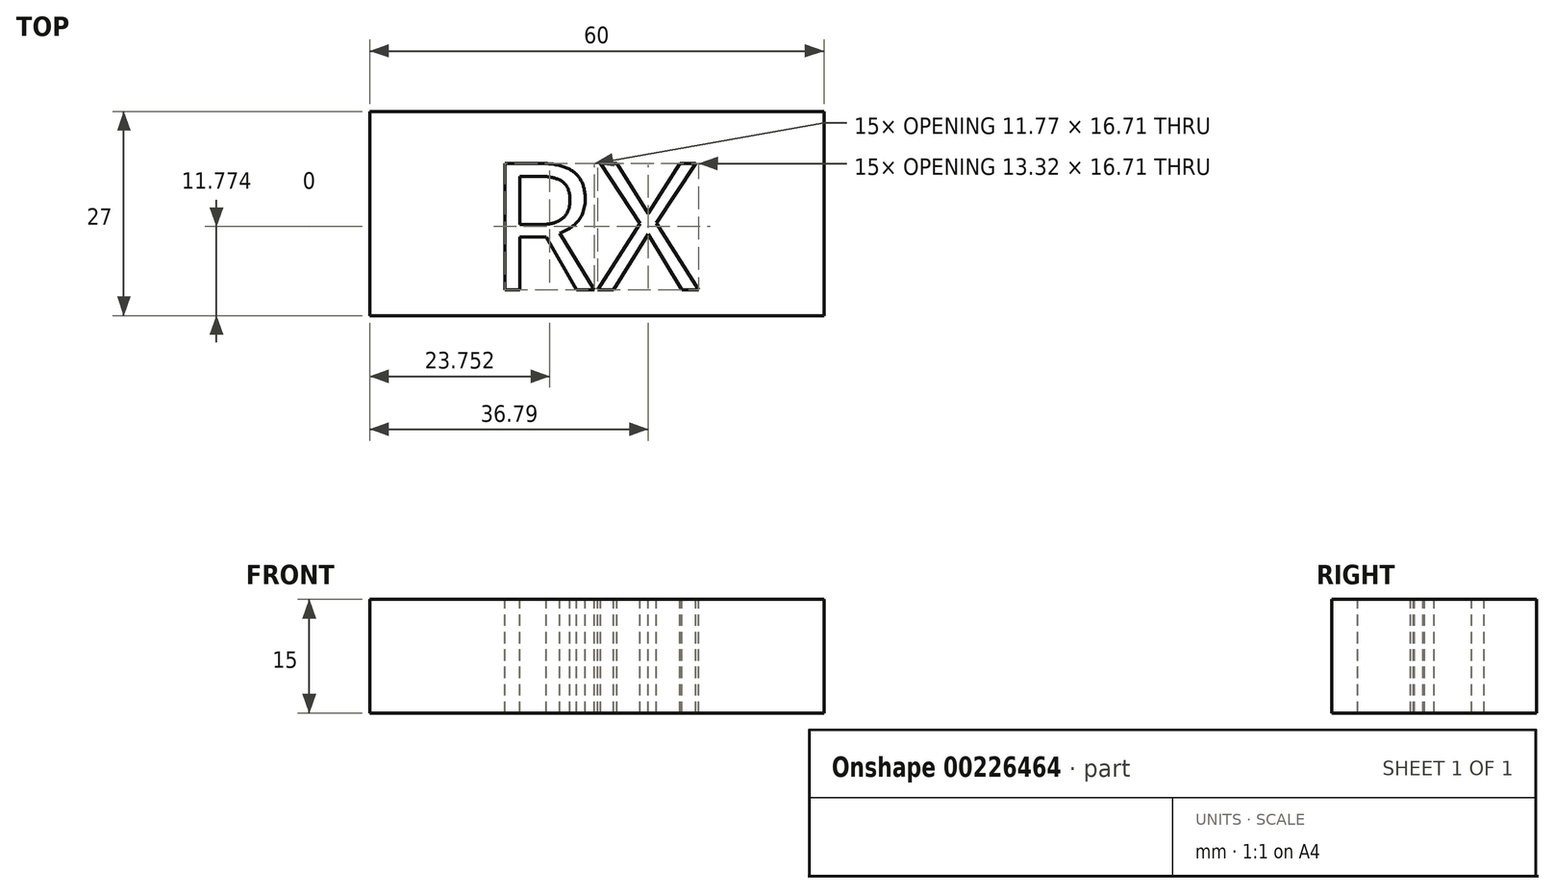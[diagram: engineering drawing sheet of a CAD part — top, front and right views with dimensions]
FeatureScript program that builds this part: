
annotation { "Feature Type Name" : "Feature", "Feature Type Description" : "" }
export const myFeature = defineFeature(function(context is Context, id is Id, definition is map)
    precondition{}
    {
        {
            var Q0;
            Q0=qCreatedBy(makeId("Top.planeOp"),FACE);
            var sketch = newSketch(context, id + "F0", { "sketchPlane" : qUnion([Q0])});
            skLineSegment(sketch, "E0.bottom", {"start": v(30, 13.5) * mm, "end": v(-30, 13.5) * mm});
            skLineSegment(sketch, "E0.top", {"start": v(30, -13.5) * mm, "end": v(-30, -13.5) * mm});
            skLineSegment(sketch, "E0.left", {"start": v(30, 13.5) * mm, "end": v(30, -13.5) * mm});
            skLineSegment(sketch, "E0.right", {"start": v(-30, 13.5) * mm, "end": v(-30, -13.5) * mm});
            skPoint(sketch, "E0.middle", {"position": v(0, 0) * mm});
            skSolve(sketch);
        }
        {
            var Q0;
            Q0=makeQuery(id+"F0.imprint","IMPRINT",FACE,{"disambiguationData":[TD([[makeQuery(id+"F0.imprint","IMPRINT",EDGE,{"derivedFrom":sQuery(id+"F0.wireOp",EDGE,"E0.bottom")}),1.0]])]});
            extrude(context, id + "F1", {"entities" : qUnion([Q0]), "depth" : 15 * mm});
        }
        {
            var Q0;
            Q0=makeQuery(id+"F1.opExtrude","CAP_FACE",FACE,{"disambiguationData":[OSD([sQuery(id+"F0.wireOp",EDGE,"E0.bottom"),sQuery(id+"F0.wireOp",EDGE,"E0.top"),sQuery(id+"F0.wireOp",EDGE,"E0.left"),sQuery(id+"F0.wireOp",EDGE,"E0.right")])],"isStart":false});
            var sketch = newSketch(context, id + "F2", { "sketchPlane" : qUnion([Q0])});
            skText(sketch, "E1", { "text": "RX", "fontName": "OpenSans-Regular.ttf"});
            const initialGuessF2  = {"E1": [-0.01443, -0.01008, 1, 0, 0.01685]};
            skSetInitialGuess(sketch, initialGuessF2);
            skSolve(sketch);
        }
        {
            var Q0;
            Q0 = qSketchRegion(id + "F2", true);
            extrude(context, id + "F3", {"entities" : qUnion([Q0]), "operationType" : NewBodyOperationType.REMOVE, "oppositeDirection" : true, "depth" : 25.4 * mm});
        }
    });
